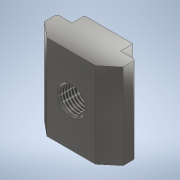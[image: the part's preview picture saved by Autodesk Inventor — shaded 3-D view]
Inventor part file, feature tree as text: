
AUTODESK INVENTOR PART (.ipt)
format: ipt  version: 2022 (Build 260153000, 153)  size: 153,600 bytes
history: native  units: mm
features: sketch x4, extrude x3, fillet x2, other x1, hole x1, chamfer x1, thread x1
ambient origin geometry x8: Origin, YZ Plane, XZ Plane, XY Plane, X Axis, Y Axis, Z Axis, Center Point
bodies: Body1 (feature_tree), Body2 (feature_tree), Body3 (feature_tree)
feature tree (13):
  other  "Твердое тело1"
  extrude  "Выдавливание1"  Depth=9.4mm
  extrude  "Выдавливание2"  Depth=4.5mm
  extrude  "Выдавливание3"  Depth=10.2mm TaperAngle=0.0deg
  hole  "Отверстие1"  [1 undecoded]
  chamfer  "Фаска1"  Distance=2.9mm
  fillet  "Сопряжение2"  Radius=5.8mm
  fillet  "Сопряжение3"  Radius=10.2mm
  thread  "Резьба2"
  sketch  "Эскиз1"
  sketch  "Эскиз3"
  sketch  "Эскиз5"
  sketch  "Эскиз6"
note: 1 required parameter value undecoded (feature->parameter linkage not recoverable at this tier; creation-order binding heuristic only, values carry confidence <= 0.55)
